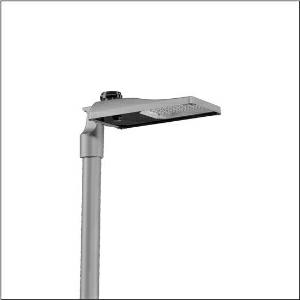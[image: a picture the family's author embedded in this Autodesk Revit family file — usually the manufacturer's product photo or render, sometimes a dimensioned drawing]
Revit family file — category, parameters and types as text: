
# Revit family: streetlight_sl_31_mini___st1_0a_5xh6d35m08ha_c080
name_source: partatom
category: Lighting Fixtures
units: mm (PartAtom-declared; Revit-internal decimal feet)

## family parameters
Cut with Voids When Loaded = No
Host = Face
Light Source = No
Part Type = Normal
Room Calculation Point = No
Round Connector Dimension = Use Diameter
Shared = No

## types (1)
- --- (1 x LED, 9230 lm, 68.3 W, 3000K)
    Apparent Load = 68 VA
    CIE Flux Codes = 37 72 97 100 100
    Color Rendering = 70
    Color Temperature = 3000K
    Default Elevation = 1800 mm
    Description = Streetlight SL 31 mini NEMA (7pin), Desk-Remote mast luminaire for post-top, side-entry; light control with lens of PMMA; light distribution: ST1.0a, direct asymmetric distribution, for standard-compliant lighting for roads and squares; LED: luminous flux: 9.230lm, light colour: 730, colour temperature: 3000K; luminous efficacy: 135,1lm/W; control: pre-setting: linear dimming characteristic, flexible luminous flux parameterisation, time-dependent luminous flux control, constant luminous flux control, intelligent temperature release in ECG and LED module, overheat protection; luminaire housing, of diecast aluminium, Siteco® metallic grey (DB 702S), corrosivity category C5 high according to DIN EN ISO 12944; cover of toughened safety glass, transparent, opened without tools; mast flange of diecast aluminium, Siteco® metallic grey (DB 702S), spigot size: 76/60mm, mast flange included unmounted; with cable H07RN-F 3x 1.5mm², cable length: 8,5m, connection cable pre-assembled; mains connection: 220..240V, AC, 50/60Hz; power consumption (at start of service life): 68,3W / (at end of service life): 74,5W / (with reduced operation 50%): 29,5W; protection rating (complete): IP66; insulation class (complete): insulation class I (protective earthing); impact resistance: IK09; certification: CE, ENEC, ENEC+, VDE, UKCA; permissible operating ambient temperature for outdoor applications: -40..+50°C; packaging unit: 1 piece

Light Distribution: ST1.0a
    Height = 76 mm
    Lamp = 1 x LED
    Lamp Light Flux = 9230 lm
    Lamp Power = 68.3 W
    Lamp count = 1
    Length = 547 mm
    Luminous efficacy = 135 lm/W
    Manufacturer = Siteco
    ModVariant = No
    Model = 5XH6D35M08HA
    Number of Poles = 1
    OnlyDefault = Yes
    Power Factor = 1
    Product Name = Streetlight SL 31 mini | ST1.0a
    Product group = mast luminaire | pylon top
    ProductGroupID = 6100
    Protection Class = Protection class I
    Protection Degree = IP 66
    RLX_Detail_Level = 1
    RLX_Emergency_Light_Flux = 0 lm
    RLX_Emergency_Type = 0
    RLX_Emergency_Type_DB = No
    RlxData = <blob elided: 24865 chars, md5=edde5960>
    Socket = socket
    Standby Power = 0 W
    System Light Flux = 9230 lm
    System Power = 68 W
    Type Comments = factory setting: luminous flux: 100 % | dim-lin: 254 | 692 mA
    Type Image = l_1300324.jpg
    URL = http://relux.com
    VarID = @adj_019113
    Voltage = 0 V
    Weight = 0.00 kg
    Width = 265 mm

## geometry (parser evidence)
native form markers: Blend x4, Sweep x9
no freeform markers — native parametric forms only
